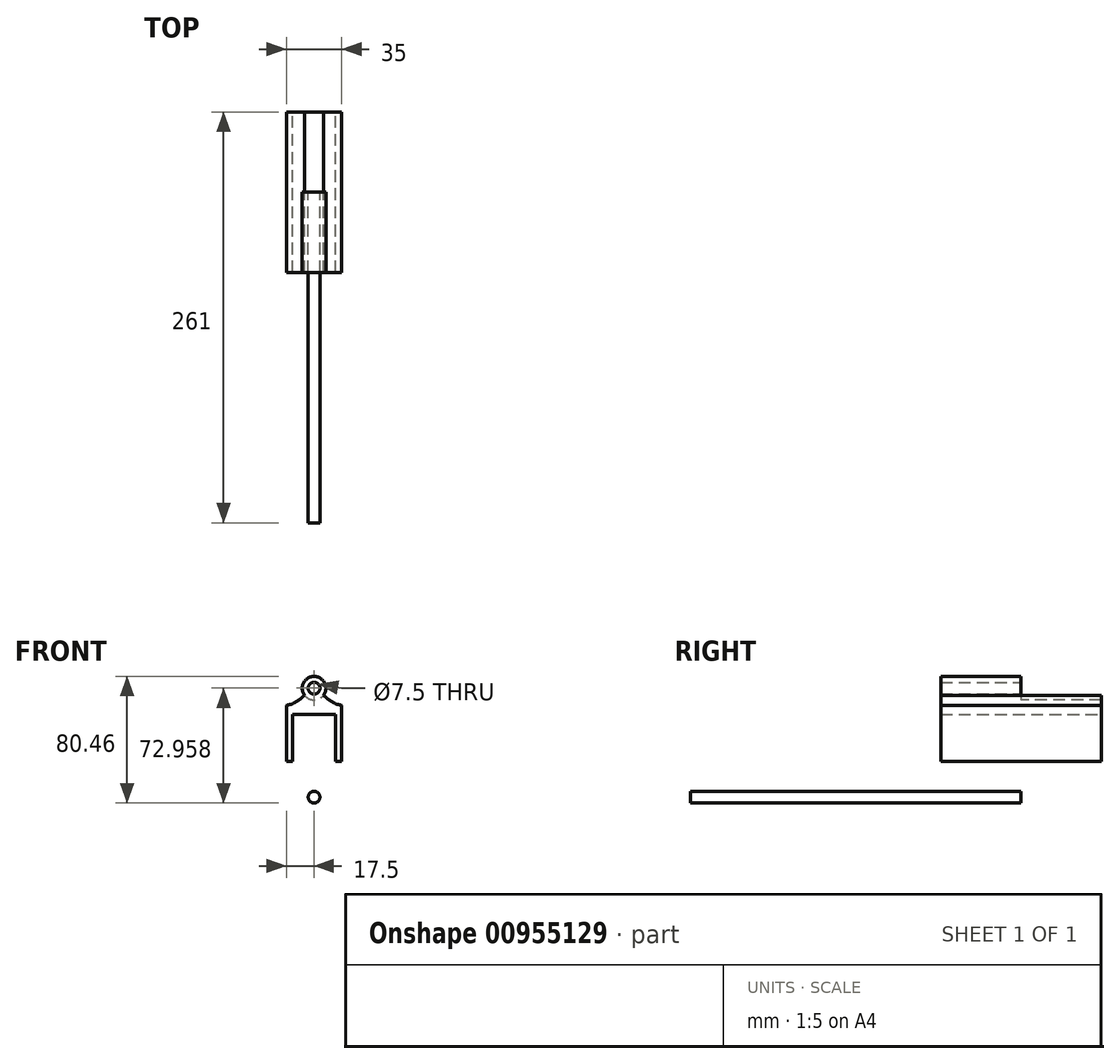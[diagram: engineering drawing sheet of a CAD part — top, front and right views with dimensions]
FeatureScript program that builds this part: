
annotation { "Feature Type Name" : "Feature", "Feature Type Description" : "" }
export const myFeature = defineFeature(function(context is Context, id is Id, definition is map)
    precondition{}
    {
        {
            var Q0;
            Q0=qCreatedBy(makeId("Front.planeOp"),FACE);
            var sketch = newSketch(context, id + "F0", { "sketchPlane" : qUnion([Q0])});
            skCircle(sketch, "E0", {"center": v(0, 48.86) * mm, "radius": 7.5 * mm});
            skLineSegment(sketch, "E1.left", {"start": v(17.5, 2.27) * mm, "end": v(17.5, 38.04) * mm});
            skLineSegment(sketch, "E1.right", {"start": v(-17.5, 2.27) * mm, "end": v(-17.5, 38.04) * mm});
            skPoint(sketch, "E1.middle", {"position": v(0, 20.16) * mm});
            skLineSegment(sketch, "E2", {"start": v(-17.5, 2.27) * mm, "end": v(-13.5, 2.27) * mm});
            skLineSegment(sketch, "E3", {"start": v(17.5, 2.27) * mm, "end": v(13.5, 2.27) * mm});
            skLineSegment(sketch, "E4", {"start": v(-13.5, 2.27) * mm, "end": v(-13.5, 32.27) * mm});
            skLineSegment(sketch, "E5", {"start": v(13.5, 2.27) * mm, "end": v(13.5, 32.27) * mm});
            skLineSegment(sketch, "E6", {"start": v(-13.5, 32.27) * mm, "end": v(13.5, 32.27) * mm});
            skFitSpline(sketch, "E7", {"points": [v(-6, 44.36) * mm, v(-12.48, 39.5) * mm, v(-17.5, 38.04) * mm], "startDerivative": vector(-11.77, -10.25) * mm, "endDerivative": vector(-11.16, -2.06) * mm});
            skFitSpline(sketch, "E8.MirrorCS", {"points": [v(6, 44.36) * mm, v(12.48, 39.5) * mm, v(17.5, 38.04) * mm], "startDerivative": vector(11.77, -10.25) * mm, "endDerivative": vector(11.16, -2.06) * mm});
            skCircle(sketch, "E9", {"center": v(0, -20.4) * mm, "radius": 3.7 * mm});
            skSolve(sketch);
        }
        {
            var Q0;
            Q0=makeQuery(id+"F0.imprint","IMPRINT",FACE,{"disambiguationData":[TD([[makeQuery(id+"F0.imprint","IMPRINT",EDGE,{"derivedFrom":sQuery(id+"F0.wireOp",EDGE,"E1.left")}),1.0]])]});
            var Q1;
            {var subQ0=sQuery(id+"F0.wireOp",EDGE,"E0");var subQ1=makeQuery(id+"F0.imprint","INTERSECT",VERTEX,{"derivedFrom":[subQ0,sQuery(id+"F0.wireOp",EDGE,"E7")]});Q1=makeQuery(id+"F0.imprint","IMPRINT",FACE,{"disambiguationData":[TD([[makeQuery(id+"F0.imprint","IMPRINT",EDGE,{"disambiguationData":[TD([[subQ1,-1.0]])],"derivedFrom":subQ0}),1.0]])]});}
            extrude(context, id + "F1", {"entities" : qUnion([Q0, Q1]), "depth" : 51 * mm, "offsetDistance" : 25 * mm});
        }
        {
            var Q0;
            Q0=makeQuery(id+"F0.imprint","IMPRINT",FACE,{"disambiguationData":[TD([[makeQuery(id+"F0.imprint","IMPRINT",EDGE,{"derivedFrom":sQuery(id+"F0.wireOp",EDGE,"E1.left")}),1.0]])]});
            extrude(context, id + "F2", {"entities" : qUnion([Q0]), "operationType" : NewBodyOperationType.ADD, "depth" : 51 * mm, "offsetDistance" : 25 * mm});
        }
        {
            var Q0;
            Q0=makeQuery(id+"F0.imprint","IMPRINT",FACE,{"disambiguationData":[TD([[makeQuery(id+"F0.imprint","IMPRINT",EDGE,{"derivedFrom":sQuery(id+"F0.wireOp",EDGE,"E1.left")}),1.0]])]});
            extrude(context, id + "F3", {"entities" : qUnion([Q0]), "operationType" : NewBodyOperationType.ADD, "oppositeDirection" : true, "depth" : 51 * mm, "offsetDistance" : 25 * mm});
        }
        {
            var Q0;
            Q0=sQuery(id+"F0.wireOp",VERTEX,"E0.center");
            var Q1;
            Q1=makeQuery(id+"F1.opExtrude","SWEPT_BODY",BODY,{"disambiguationData":[OSD([sQuery(id+"F0.wireOp",EDGE,"E0"),sQuery(id+"F0.wireOp",EDGE,"E1.left"),sQuery(id+"F0.wireOp",EDGE,"E1.right"),sQuery(id+"F0.wireOp",EDGE,"E2"),sQuery(id+"F0.wireOp",EDGE,"E3"),sQuery(id+"F0.wireOp",EDGE,"E4"),sQuery(id+"F0.wireOp",EDGE,"E5"),sQuery(id+"F0.wireOp",EDGE,"E6"),sQuery(id+"F0.wireOp",EDGE,"E7"),sQuery(id+"F0.wireOp",EDGE,"E8.MirrorCS")])]});
            hole(context, id + "F4", {"style" : HoleStyle.SIMPLE, "endStyle" : HoleEndStyle.THROUGH, "oppositeDirection" : true, "holeDiameter" : 7.5 * mm, "majorDiameter" : 5 * mm, "isTappedThrough" : true, "tappedDepth" : 12 * mm, "tapClearance" : 3, "locations" : qUnion([Q0]), "scope" : qUnion([Q1])});
        }
        {
            var Q0;
            Q0=makeQuery(id+"F0.imprint","IMPRINT",FACE,{"disambiguationData":[TD([[makeQuery(id+"F0.imprint","IMPRINT",EDGE,{"derivedFrom":sQuery(id+"F0.wireOp",EDGE,"E9")}),1.0]])]});
            extrude(context, id + "F5", {"entities" : qUnion([Q0]), "depth" : 210 * mm, "offsetDistance" : 25 * mm});
        }
    });
